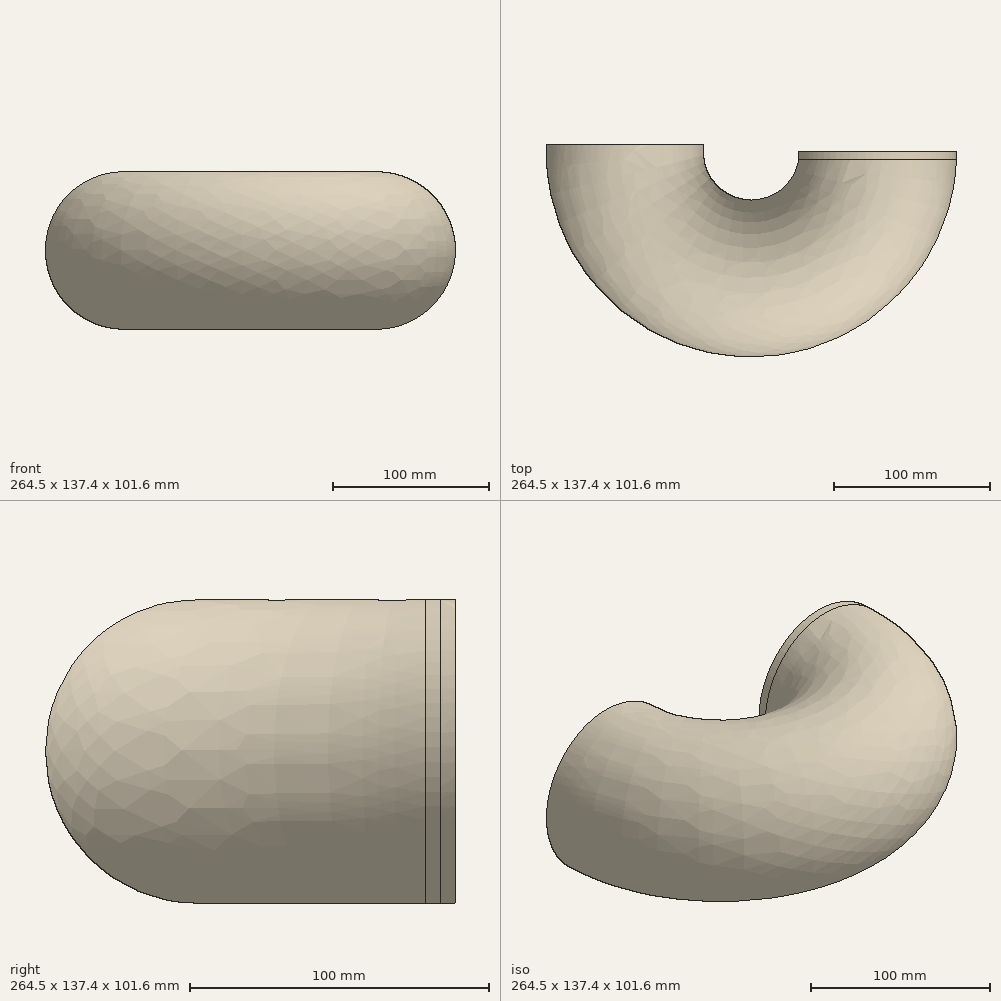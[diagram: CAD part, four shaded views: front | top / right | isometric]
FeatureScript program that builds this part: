
annotation { "Feature Type Name" : "Feature", "Feature Type Description" : "" }
export const myFeature = defineFeature(function(context is Context, id is Id, definition is map)
    precondition{}
    {
        {
            var Q0;
            Q0=qCreatedBy(makeId("Front.planeOp"),FACE);
            var sketch = newSketch(context, id + "F0", { "sketchPlane" : qUnion([Q0])});
            skCircle(sketch, "E0", {"center": v(81.41, 0) * mm, "radius": 50.8 * mm});
            skLineSegment(sketch, "E1", {"start": v(0, 0) * mm, "end": v(0, -51.5) * mm, "construction": true});
            skLineSegment(sketch, "E2", {"start": v(0, 0) * mm, "end": v(0, 49.97) * mm, "construction": true});
            skCircle(sketch, "E3", {"center": v(81.41, 0) * mm, "radius": 46.13 * mm});
            skSolve(sketch);
        }
        {
            var Q0;
            Q0=makeQuery(id+"F0.imprint","IMPRINT",FACE,{"disambiguationData":[TD([[makeQuery(id+"F0.imprint","IMPRINT",EDGE,{"derivedFrom":sQuery(id+"F0.wireOp",EDGE,"E0")}),1.0]])]});
            extrude(context, id + "F1", {"entities" : qUnion([Q0]), "depth" : 5.08 * mm, "offsetDistance" : 25.4 * mm});
        }
        {
            var Q0;
            Q0=makeQuery(id+"F1.opExtrude","CAP_FACE",FACE,{"disambiguationData":[OSD([sQuery(id+"F0.wireOp",EDGE,"E0"),sQuery(id+"F0.wireOp",EDGE,"E3")])],"isStart":false});
            var Q1;
            Q1=sQuery(id+"F0.wireOp",EDGE,"E1");
            revolve(context, id + "F2", {"operationType" : NewBodyOperationType.ADD, "surfaceOperationType" : NewSurfaceOperationType.NEW, "entities" : qUnion([Q0]), "axis" : qUnion([Q1]), "revolveType" : RevolveType.ONE_DIRECTION, "angle" : 180 * degree});
        }
    });
